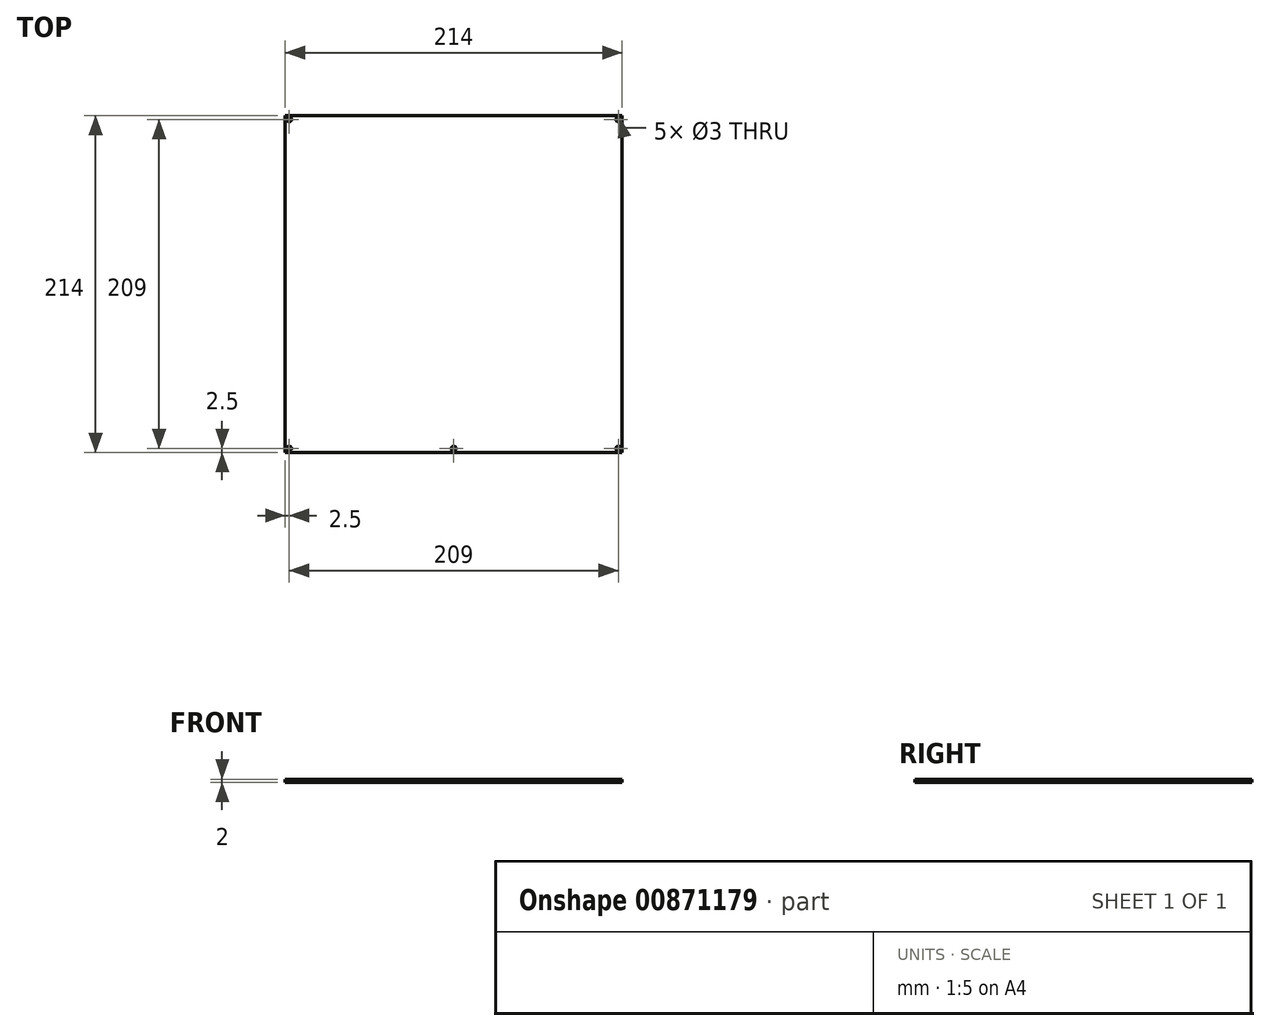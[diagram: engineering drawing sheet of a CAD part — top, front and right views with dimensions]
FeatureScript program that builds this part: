
annotation { "Feature Type Name" : "Feature", "Feature Type Description" : "" }
export const myFeature = defineFeature(function(context is Context, id is Id, definition is map)
    precondition{}
    {
        {
            var Q0;
            Q0=qCreatedBy(makeId("Top.planeOp"),FACE);
            var sketch = newSketch(context, id + "F0", { "sketchPlane" : qUnion([Q0])});
            skLineSegment(sketch, "E0.bottom", {"start": v(107, -107) * mm, "end": v(-107, -107) * mm});
            skLineSegment(sketch, "E0.top", {"start": v(107, 107) * mm, "end": v(-107, 107) * mm});
            skLineSegment(sketch, "E0.left", {"start": v(107, -107) * mm, "end": v(107, 107) * mm});
            skLineSegment(sketch, "E0.right", {"start": v(-107, -107) * mm, "end": v(-107, 107) * mm});
            skPoint(sketch, "E0.middle", {"position": v(0, 0) * mm});
            skLineSegment(sketch, "E1.bottom", {"start": v(104.5, -104.5) * mm, "end": v(-104.5, -104.5) * mm, "construction": true});
            skLineSegment(sketch, "E1.top", {"start": v(104.5, 104.5) * mm, "end": v(-104.5, 104.5) * mm, "construction": true});
            skLineSegment(sketch, "E1.left", {"start": v(104.5, -104.5) * mm, "end": v(104.5, 104.5) * mm, "construction": true});
            skLineSegment(sketch, "E1.right", {"start": v(-104.5, -104.5) * mm, "end": v(-104.5, 104.5) * mm, "construction": true});
            skCircle(sketch, "E2", {"center": v(-104.5, 104.5) * mm, "radius": 1.5 * mm});
            skCircle(sketch, "E3", {"center": v(104.5, 104.5) * mm, "radius": 1.5 * mm});
            skCircle(sketch, "E4", {"center": v(104.5, -104.5) * mm, "radius": 1.5 * mm});
            skCircle(sketch, "E5", {"center": v(-104.5, -104.5) * mm, "radius": 1.5 * mm});
            skCircle(sketch, "E6", {"center": v(0, -104.5) * mm, "radius": 1.5 * mm});
            skSolve(sketch);
        }
        {
            var Q0;
            Q0 = qSketchRegion(id + "F0", true);
            extrude(context, id + "F1", {"entities" : qUnion([Q0]), "depth" : 2 * mm, "offsetDistance" : 25 * mm});
        }
    });
